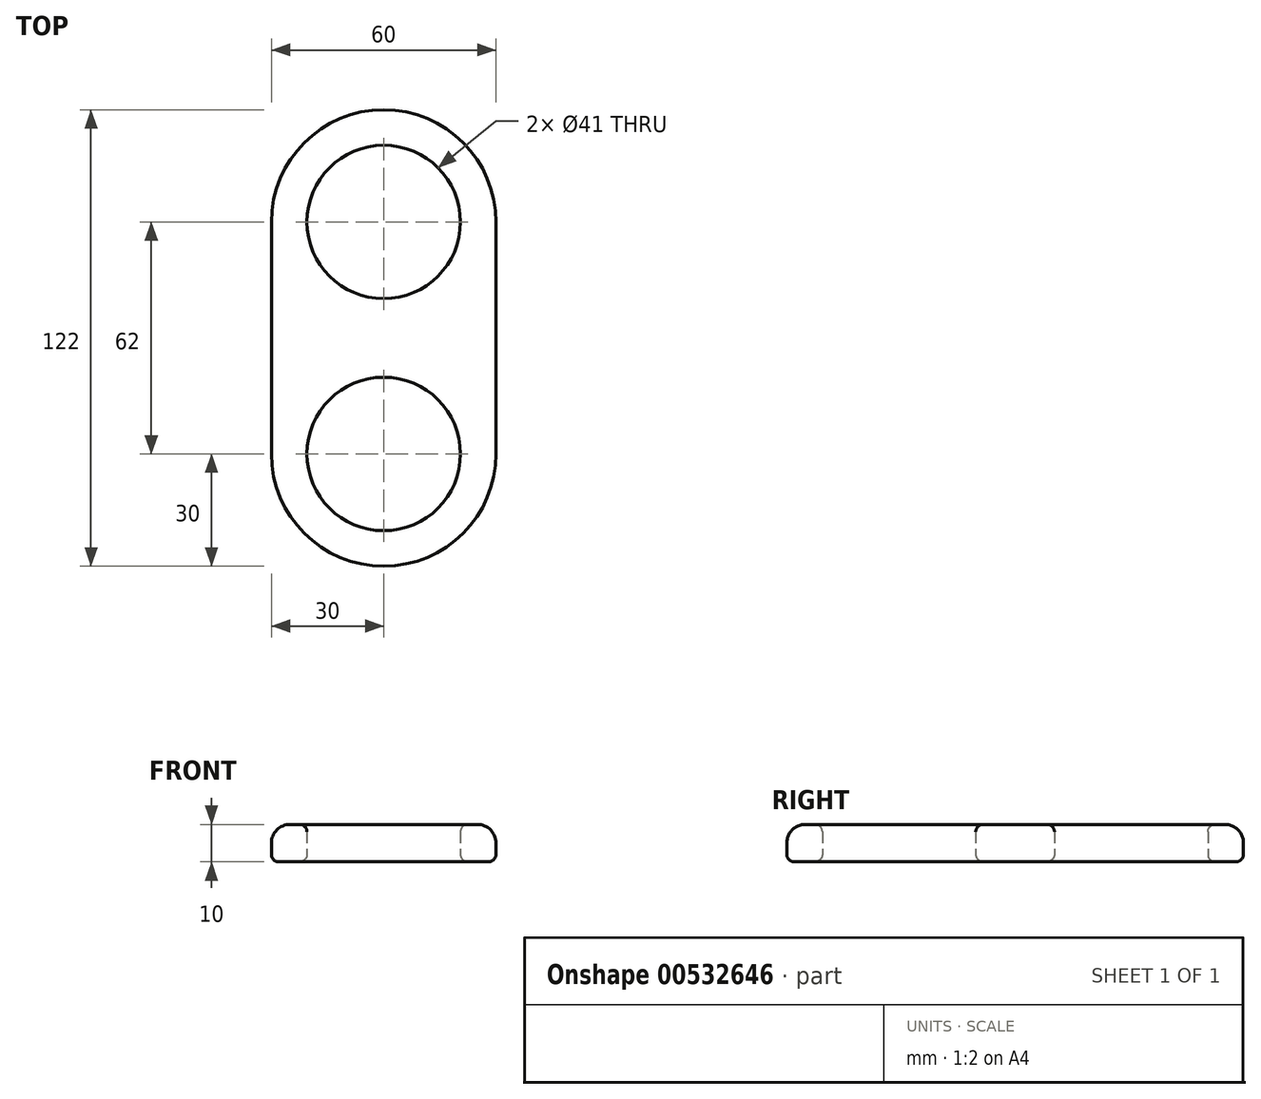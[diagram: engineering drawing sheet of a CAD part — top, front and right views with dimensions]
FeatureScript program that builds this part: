
annotation { "Feature Type Name" : "Feature", "Feature Type Description" : "" }
export const myFeature = defineFeature(function(context is Context, id is Id, definition is map)
    precondition{}
    {
        {
            var Q0;
            Q0=qCreatedBy(makeId("Top.planeOp"),FACE);
            var sketch = newSketch(context, id + "F0", { "sketchPlane" : qUnion([Q0])});
            skLineSegment(sketch, "E0", {"start": v(0, 31) * mm, "end": v(0, -31) * mm});
            skArc(sketch, "E1.0.startCap", {"start": v(-30, 31) * mm, "mid": v(0, 61) * mm, "end": v(30, 31) * mm});
            skArc(sketch, "E1.0.endCap", {"start": v(30, -31) * mm, "mid": v(0, -61) * mm, "end": v(-30, -31) * mm});
            skLineSegment(sketch, "E1.0.left", {"start": v(30, 31) * mm, "end": v(30, -31) * mm});
            skLineSegment(sketch, "E1.0.right", {"start": v(-30, 31) * mm, "end": v(-30, -31) * mm});
            skCircle(sketch, "E2", {"center": v(0, 31) * mm, "radius": 20.5 * mm});
            skCircle(sketch, "E3.1.0", {"center": v(0, -31) * mm, "radius": 20.5 * mm});
            skPoint(sketch, "E3.center", {"position": v(0, 0) * mm});
            skSolve(sketch);
        }
        {
            var Q0;
            Q0 = qSketchRegion(id + "F0", true);
            extrude(context, id + "F1", {"entities" : qUnion([Q0]), "depth" : 10 * mm, "offsetDistance" : 25 * mm});
        }
        {
            var Q0;
            Q0=makeQuery(id+"F1.opExtrude","CAP_EDGE",EDGE,{"disambiguationData":[OSD([sQuery(id+"F0.wireOp",EDGE,"E2")])],"isStart":false});
            var Q1;
            Q1=makeQuery(id+"F1.opExtrude","CAP_EDGE",EDGE,{"disambiguationData":[OSD([sQuery(id+"F0.wireOp",EDGE,"E2")])],"isStart":true});
            var Q2;
            Q2=makeQuery(id+"F1.opExtrude","CAP_EDGE",EDGE,{"disambiguationData":[OSD([sQuery(id+"F0.wireOp",EDGE,"E3.1.0")])],"isStart":false});
            var Q3;
            Q3=makeQuery(id+"F1.opExtrude","CAP_EDGE",EDGE,{"disambiguationData":[OSD([sQuery(id+"F0.wireOp",EDGE,"E3.1.0")])],"isStart":true});
            var Q4;
            Q4=makeQuery(id+"F1.opExtrude","CAP_EDGE",EDGE,{"disambiguationData":[OSD([sQuery(id+"F0.wireOp",EDGE,"E1.0.left")])],"isStart":true});
            fillet(context, id + "F2", {"entities" : qUnion([Q0, Q1, Q2, Q3, Q4]), "radius" : 2 * mm, "tangentPropagation" : true, "allowEdgeOverflow" : false});
        }
        {
            var Q0;
            Q0=makeQuery(id+"F1.opExtrude","CAP_EDGE",EDGE,{"disambiguationData":[OSD([sQuery(id+"F0.wireOp",EDGE,"E1.0.right")])],"isStart":false});
            fillet(context, id + "F3", {"entities" : qUnion([Q0]), "radius" : 5 * mm, "tangentPropagation" : true, "allowEdgeOverflow" : false});
        }
    });
